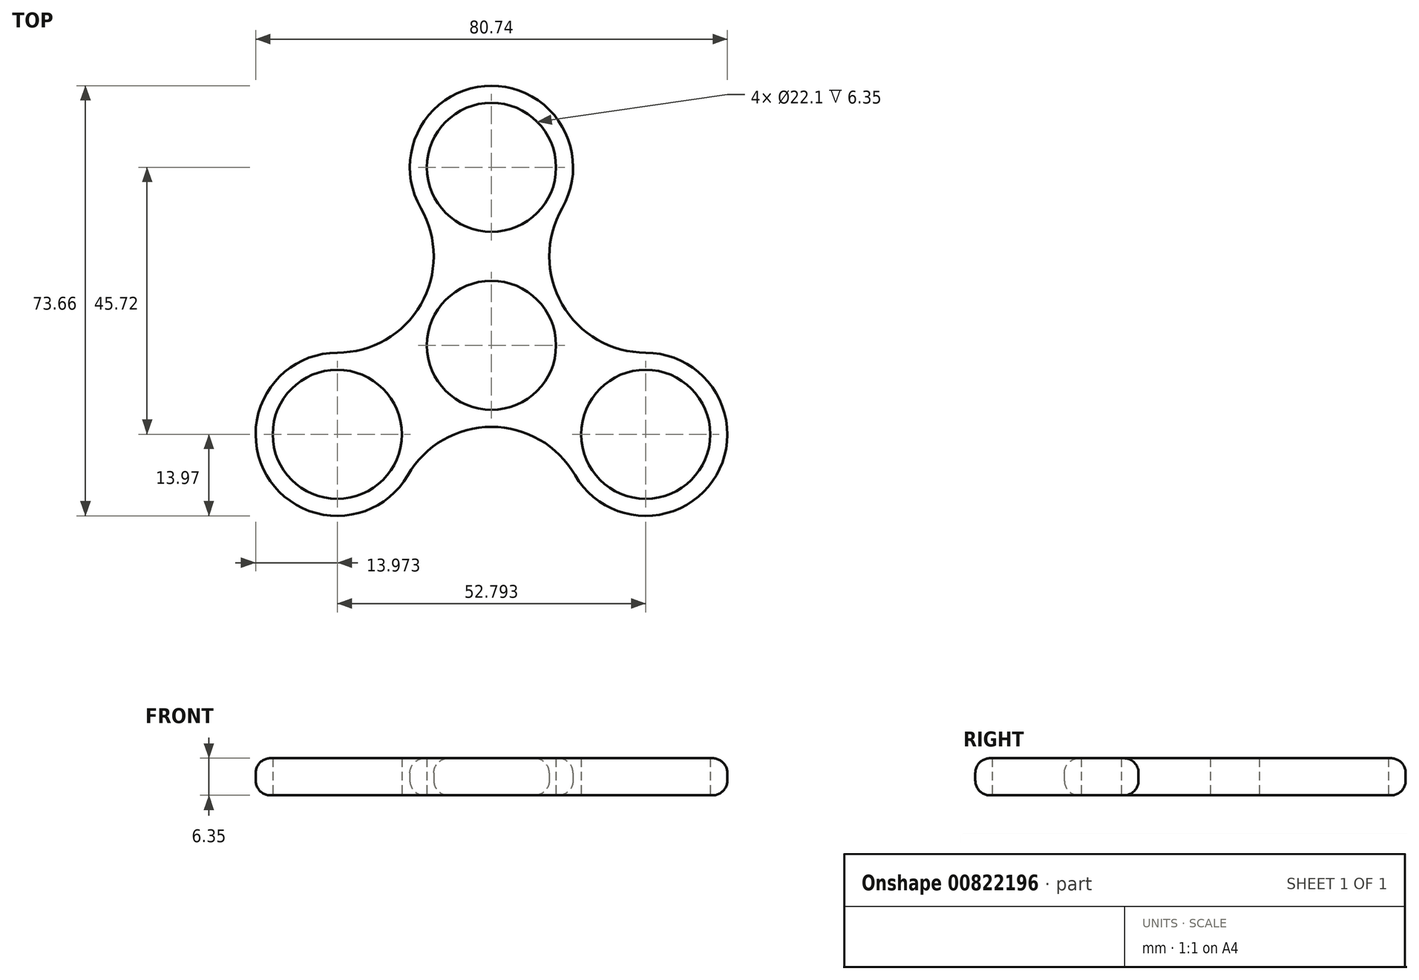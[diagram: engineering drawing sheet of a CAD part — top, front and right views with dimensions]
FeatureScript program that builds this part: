
annotation { "Feature Type Name" : "Feature", "Feature Type Description" : "" }
export const myFeature = defineFeature(function(context is Context, id is Id, definition is map)
    precondition{}
    {
        {
            var Q0;
            Q0=qCreatedBy(makeId("Top.planeOp"),FACE);
            var sketch = newSketch(context, id + "F0", { "sketchPlane" : qUnion([Q0])});
            skCircle(sketch, "E0", {"center": v(0, 0) * mm, "radius": 11.05 * mm});
            skCircle(sketch, "E1", {"center": v(0, 0) * mm, "radius": 13.97 * mm});
            skCircle(sketch, "E2", {"center": v(0, 30.48) * mm, "radius": 11.05 * mm});
            skCircle(sketch, "E3", {"center": v(0, 30.48) * mm, "radius": 13.97 * mm});
            skCircle(sketch, "E4.1.0", {"center": v(-26.4, -15.24) * mm, "radius": 11.05 * mm});
            skCircle(sketch, "E4.1.1", {"center": v(-26.4, -15.24) * mm, "radius": 13.97 * mm});
            skCircle(sketch, "E4.2.0", {"center": v(26.4, -15.24) * mm, "radius": 11.05 * mm});
            skCircle(sketch, "E4.2.1", {"center": v(26.4, -15.24) * mm, "radius": 13.97 * mm});
            skArc(sketch, "E5", {"start": v(-26.4, -1.27) * mm, "mid": v(-12.1, 6.98) * mm, "end": v(-12.1, 23.5) * mm});
            skArc(sketch, "E6.1.0", {"start": v(14.3, -22.22) * mm, "mid": v(0, -13.97) * mm, "end": v(-14.3, -22.22) * mm});
            skArc(sketch, "E6.2.0", {"start": v(12.1, 23.5) * mm, "mid": v(12.1, 6.98) * mm, "end": v(26.4, -1.27) * mm});
            skSolve(sketch);
        }
        {
            var Q0;
            Q0 = qSketchRegion(id + "F0", true);
            extrude(context, id + "F1", {"entities" : qUnion([Q0]), "depth" : 6.35 * mm, "offsetDistance" : 25.4 * mm});
        }
        {
            var Q0;
            Q0=makeQuery(id+"F1.opExtrude","CAP_EDGE",EDGE,{"disambiguationData":[OSD([sQuery(id+"F0.wireOp",EDGE,"E6.1.0")])],"isStart":false});
            fillet(context, id + "F2", {"entities" : qUnion([Q0]), "radius" : 2.54 * mm, "tangentPropagation" : true, "allowEdgeOverflow" : false});
        }
        {
            var Q0;
            Q0=makeQuery(id+"F1.opExtrude","CAP_EDGE",EDGE,{"disambiguationData":[OSD([sQuery(id+"F0.wireOp",EDGE,"E5")])],"isStart":true});
            fillet(context, id + "F3", {"entities" : qUnion([Q0]), "radius" : 2.54 * mm, "tangentPropagation" : true, "allowEdgeOverflow" : false});
        }
    });
